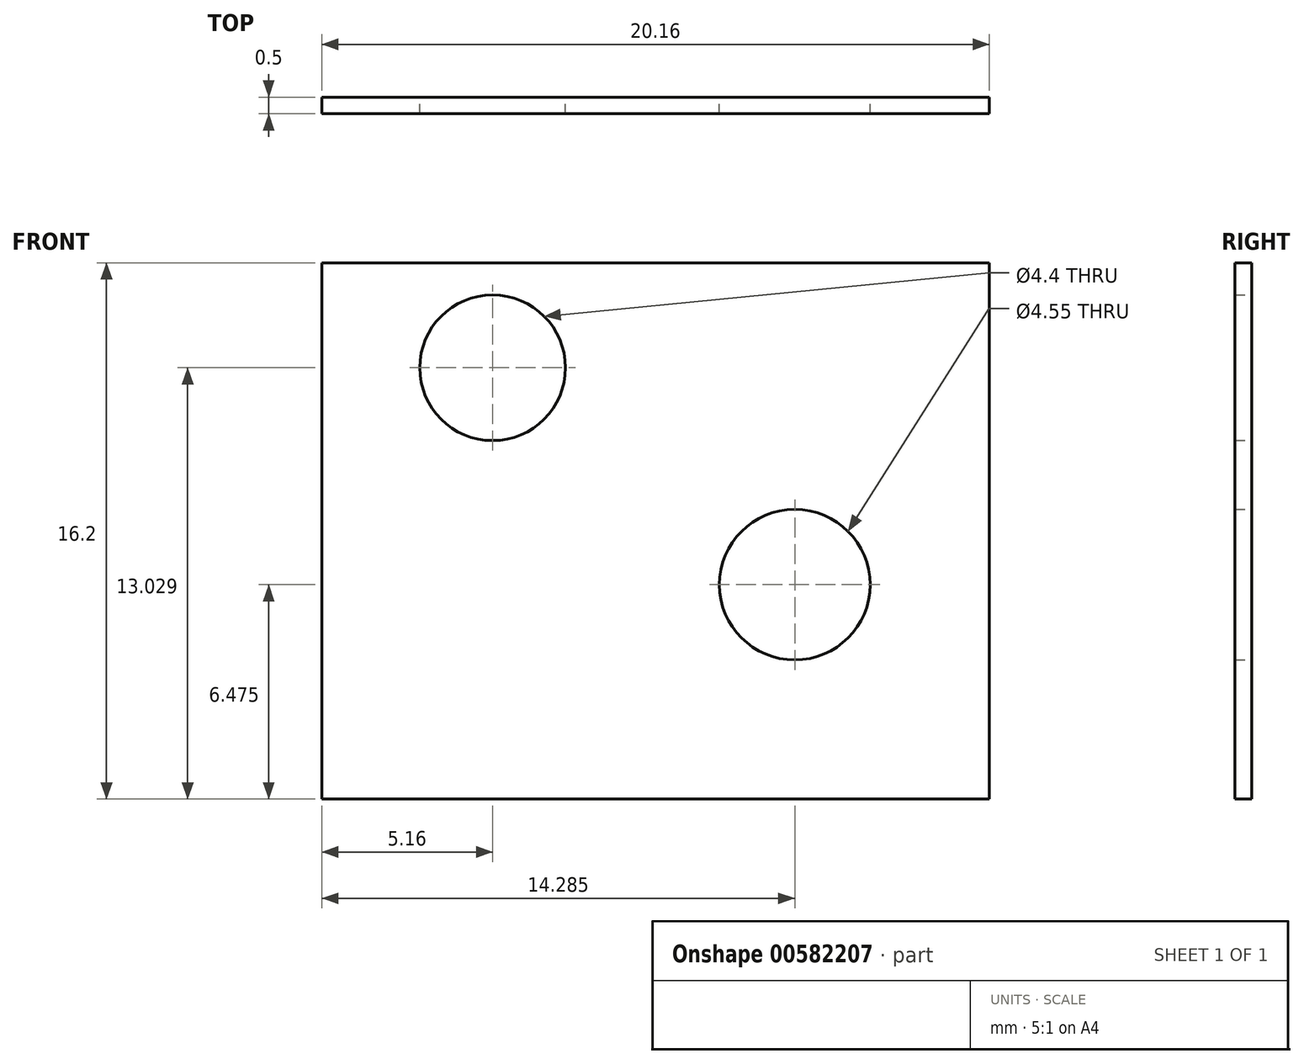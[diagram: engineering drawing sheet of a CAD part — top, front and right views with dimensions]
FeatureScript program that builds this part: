
annotation { "Feature Type Name" : "Feature", "Feature Type Description" : "" }
export const myFeature = defineFeature(function(context is Context, id is Id, definition is map)
    precondition{}
    {
        {
            var Q0;
            Q0=qCreatedBy(makeId("Front.planeOp"),FACE);
            var sketch = newSketch(context, id + "F0", { "sketchPlane" : qUnion([Q0])});
            skLineSegment(sketch, "E0", {"start": v(-20.16, 16.2) * mm, "end": v(0, 16.2) * mm});
            skLineSegment(sketch, "E1", {"start": v(0, 16.2) * mm, "end": v(0, 0) * mm});
            skLineSegment(sketch, "E2", {"start": v(0, 0) * mm, "end": v(-20.16, 0) * mm});
            skLineSegment(sketch, "E3", {"start": v(-20.16, 0) * mm, "end": v(-20.16, 16.2) * mm});
            skCircle(sketch, "E4", {"center": v(-15, 13.03) * mm, "radius": 2.2 * mm});
            skCircle(sketch, "E5", {"center": v(-5.87, 6.48) * mm, "radius": 2.27 * mm});
            skSolve(sketch);
        }
        {
            var Q0;
            Q0=makeQuery(id+"F0.imprint","IMPRINT",FACE,{"disambiguationData":[TD([[makeQuery(id+"F0.imprint","IMPRINT",EDGE,{"derivedFrom":sQuery(id+"F0.wireOp",EDGE,"E0")}),-1.0]])]});
            extrude(context, id + "F1", {"entities" : qUnion([Q0]), "depth" : 0.5 * mm, "offsetDistance" : 25 * mm});
        }
    });
